# Revit family: WALL DOUBLE TUBE 02_AM24W.1.12
name_source: partatom
category: Luminarias
units: mm (PartAtom-declared; Revit-internal decimal feet)

## family parameters
Compartido = No
Corte con vacíos al cargar = No
Cota de conector redondo = Diámetro de uso
Origen de luz = Sí
Punto de cálculo de habitación = No
Se basa en plano de trabajo = Sí
Siempre vertical = No
Tipo de pieza = Normal

## types (1)
- WALL DOUBLE TUBE 02_AM24W.1.12
    Archivo de red fotométrica = AM24W.1_12º.IES
    Cambio de temperatura de color de luz atenuada = <Ninguno>
    Comentarios de vataje = 100-277V
    Descripción = LUMINARIA DIRIGIBLE EN FORMA TUBULAR TIPO ARBOTANTE DOBLE DE HAZ (UP & DOWN), DE MATERIAL EN ALEACION DE ALUMINIO EXTRUIDO CON UN PESO DE 2.3KG, CON 2 LED TIPO NICHIA CON UNA POTENCIA TOTAL DE 25.5W, 2X1076 LUMENES, TEMPERATURA EN BLANCO CALIDO 3000K, IRC 80, IP 65, IK10, APERTURA DE  12 GRADOS POR PROYECTO, CORRIENTE DE OPERACIÓN 210mA, CABLE DE 0.3M, ALIMENTADO A 100-277VAC
    Elevación por defecto = 0 mm  [stored 0 ft]
    Fabricante = BRILLANT
    Filtro de color = 16777215
    Lámpara = NICHIA
    Modelo = AM24W.1.12
    Watt per fixture = 25.5
    Ángulo de inclinación = 60.00°

note: [stored X ft] marks values corroborated as IEEE doubles in the binary element streams (Revit-internal decimal feet)

## geometry (parser evidence)
native form markers: Blend x2
no freeform markers — native parametric forms only
